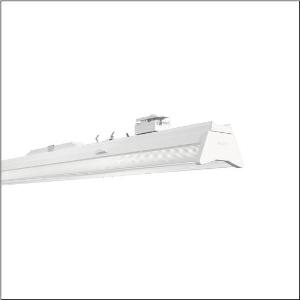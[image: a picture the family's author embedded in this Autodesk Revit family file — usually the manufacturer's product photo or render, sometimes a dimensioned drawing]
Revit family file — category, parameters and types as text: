
# Revit family: licross_r__21_performance_mo_52td16dn4a5g_459a
name_source: partatom
category: Lighting Fixtures
units: mm (PartAtom-declared; Revit-internal decimal feet)

## family parameters
Cut with Voids When Loaded = No
Host = Face
Light Source = No
Part Type = Normal
Room Calculation Point = No
Round Connector Dimension = Use Diameter
Shared = No

## types (1)
- --- (1 x LED, 10840 lm, 62 W, 4000K)
    Apparent Load = 62 VA
    CIE Flux Codes = 66 88 96 79 100
    Color Rendering = 80
    Color Temperature = 4000K
    Default Elevation = 1800 mm
    Description = Licross® 21 Performance MO, luminaire insert, of sheet steel, galvanised, coil coated, white, length: 1.500mm, width: 120mm, height: 123mm, LED rated luminous flux: 10.840lm, light colour: 840, control gear: DALI 2, with plug, 5-pole, with phase selection, mains connection: 220..240V, AC, 50/60Hz, rated input power: 62W, halogen-free wiring, primary light control with lens, of plastic, primary optical cover: cover, of PMMA, light emission: direct/indirect distribution, primary light characteristic: symmetric, protection rating (complete): IP54, insulation class (complete): insulation class I (protective earthing), certification: CE, ENEC, VDE, UKCA, protection symbol: D if used in an environment with non-conductive dust loads with corresponding accessories, impact resistance: IK06, permissible ambient temperature for indoor applications: -25..+35°C, corresponds to IFS (International Featured Standards) requirements for safety and quality in the food industry, reducing of maximum allowable ambient temperature of 5°C with ceiling mounting, LABS conformity tested according to VDMA 24364:2018-05, packaging unit: 1 piece
    Height = 114 mm
    Lamp = 1 x LED
    Lamp Light Flux = 10840 lm
    Lamp Power = 62 W
    Lamp count = 1
    Length = 1500 mm
    Luminous efficacy = 175 lm/W
    Manufacturer = Siteco
    ModVariant = No
    Model = 52TD16DN4A5G
    Mounting Place = Ceiling
    Mounting Type = Pendant
    Number of Poles = 1
    OnlyDefault = Yes
    Power Factor = 1
    Product Name = Licross® 21 Performance MO
    Product group = luminaire insert
    ProductGroupID = 901
    Protection Class = Protection class I
    Protection Degree = IP 54
    RLX_Detail_Level = 1
    RLX_Emergency_Light_Flux = 0 lm
    RLX_Emergency_Type = 0
    RLX_Emergency_Type_DB = No
    RlxData = <blob elided: 34045 chars, md5=c35b46b9>
    Socket = socket
    Standby Power = 0 W
    System Light Flux = 10840 lm
    System Power = 62 W
    Type Comments = factory setting: luminous flux: 100 % | dim-lin: 254 | 418 mA
    Type Image = l_1256138.jpg
    URL = http://relux.com
    VarID = @adj_060757
    Voltage = 0 V
    Weight = 0.00 kg
    Width = 120 mm

## geometry (parser evidence)
native form markers: Blend x4, Sweep x13
no freeform markers — native parametric forms only
